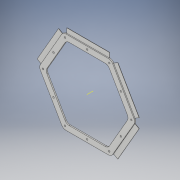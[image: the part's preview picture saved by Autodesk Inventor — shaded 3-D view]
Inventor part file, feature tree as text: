
AUTODESK INVENTOR PART (.ipt)
format: ipt  version: 2019 (Build 230136000, 136)  size: 469,504 bytes
history: native  units: mm
features: sketch x5, projected_geometry x5, extrude x4, fillet x2, other x1, pattern_circular x1, hole x1
ambient origin geometry x8: Origin, YZ Plane, XZ Plane, XY Plane, X Axis, Y Axis, Z Axis, Center Point
bodies: Solid1 (feature_tree)
feature tree (19):
  extrude  "Extrusion1"  Depth=2.0mm TaperAngle=0.0deg
  extrude  "Extrusion6"  Depth=10.0mm
  fillet  "Fillet2"  Radius=10.0mm
  fillet  "Fillet3"  Radius=12.0mm
  extrude  "Extrusion7"  Depth=0.5mm TaperAngle=0.0deg
  other  "Work Axis1"
  pattern_circular  "Circular Pattern1"  Count=6 Angle=360.0deg
  hole  "Hole1"  [1 undecoded]
  extrude  "Extrusion8"  [1 undecoded]
  sketch  "Sketch1"  dims[d0=175.0mm d1=2.0mm d2=0.0mm]
  sketch  "Sketch7"  dims[d20=7.0mm d21=0.0mm d24=10.0mm d25=10.0mm d26=12.0mm]
  projected_geometry  "Projected Loop7"
  sketch  "Sketch8"  dims[d27=10.0mm d28=0.5mm d29=0.0mm d30=60.0mm d31=360.0deg]
  projected_geometry  "Projected Loop8"
  sketch  "Sketch9"  dims[d33=60.0mm d35=360.0deg]
  projected_geometry  "Projected Loop9"
  sketch  "Sketch10"  dims[d37=3.3mm d38=6.0mm d39=10.0mm d40=2.0mm d41=90.0deg d42=26.75mm d43=0.0mm d44=10.0mm d45=0.0mm]
  projected_geometry  "Projected Loop10"
  projected_geometry  "Projected Loop11"
note: 2 required parameter values undecoded (feature->parameter linkage not recoverable at this tier; creation-order binding heuristic only, values carry confidence <= 0.55)
